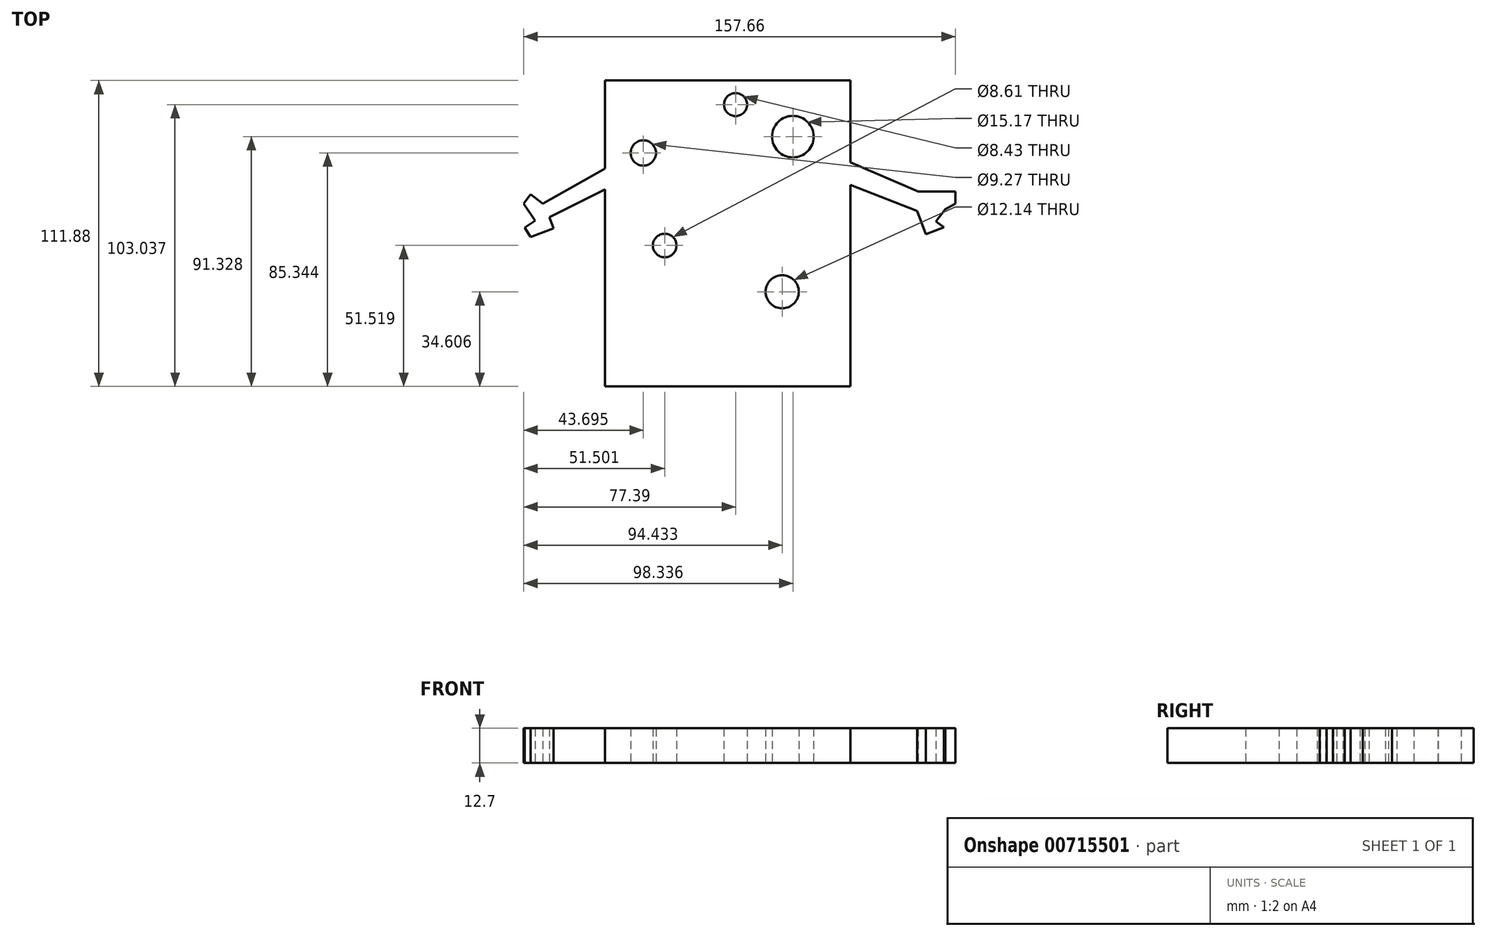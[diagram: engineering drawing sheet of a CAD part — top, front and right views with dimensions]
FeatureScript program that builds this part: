
annotation { "Feature Type Name" : "Feature", "Feature Type Description" : "" }
export const myFeature = defineFeature(function(context is Context, id is Id, definition is map)
    precondition{}
    {
        {
            var Q0;
            Q0=qCreatedBy(makeId("Top.planeOp"),FACE);
            var sketch = newSketch(context, id + "F0", { "sketchPlane" : qUnion([Q0])});
            skLineSegment(sketch, "E0.bottom", {"start": v(-47.75, 45.01) * mm, "end": v(42.02, 45.01) * mm});
            skLineSegment(sketch, "E0.top", {"start": v(-47.75, -66.87) * mm, "end": v(42.02, -66.87) * mm});
            skLineSegment(sketch, "E0.left", {"start": v(-47.75, 45.01) * mm, "end": v(-47.75, -66.87) * mm});
            skLineSegment(sketch, "E0.right", {"start": v(42.02, 45.01) * mm, "end": v(42.02, -66.87) * mm});
            skCircle(sketch, "E1", {"center": v(-33.7, 18.47) * mm, "radius": 4.63 * mm});
            skCircle(sketch, "E2", {"center": v(0, 36.17) * mm, "radius": 4.21 * mm});
            skCircle(sketch, "E3", {"center": v(20.95, 24.46) * mm, "radius": 7.59 * mm});
            skCircle(sketch, "E4", {"center": v(-25.89, -15.35) * mm, "radius": 4.3 * mm});
            skCircle(sketch, "E5", {"center": v(17.04, -32.26) * mm, "radius": 6.07 * mm});
            skLineSegment(sketch, "E6", {"start": v(-47.75, 12.75) * mm, "end": v(-70.38, 0) * mm});
            skLineSegment(sketch, "E7", {"start": v(-70.38, 0) * mm, "end": v(-74.8, 3.38) * mm});
            skLineSegment(sketch, "E8", {"start": v(-74.8, 3.38) * mm, "end": v(-77.4, 0) * mm});
            skLineSegment(sketch, "E9", {"start": v(-77.4, 0) * mm, "end": v(-73.24, -6.24) * mm});
            skLineSegment(sketch, "E10", {"start": v(-73.24, -6.24) * mm, "end": v(-77.1, -8.8) * mm});
            skLineSegment(sketch, "E11", {"start": v(-77.1, -8.8) * mm, "end": v(-74.81, -12.23) * mm});
            skLineSegment(sketch, "E12", {"start": v(-74.81, -12.23) * mm, "end": v(-66.48, -9.1) * mm});
            skLineSegment(sketch, "E13", {"start": v(-66.48, -9.1) * mm, "end": v(-68, -5.06) * mm});
            skLineSegment(sketch, "E14", {"start": v(-68, -5.06) * mm, "end": v(-47.75, 5.2) * mm});
            skLineSegment(sketch, "E15", {"start": v(42.02, 15.1) * mm, "end": v(66.74, 4.42) * mm});
            skLineSegment(sketch, "E16", {"start": v(66.74, 4.42) * mm, "end": v(80.27, 4.42) * mm});
            skLineSegment(sketch, "E17", {"start": v(80.27, 4.42) * mm, "end": v(80.27, 0) * mm});
            skLineSegment(sketch, "E18", {"start": v(80.27, 0) * mm, "end": v(76.63, -2.08) * mm});
            skLineSegment(sketch, "E19", {"start": v(76.63, -2.08) * mm, "end": v(73.24, -6.5) * mm});
            skLineSegment(sketch, "E20", {"start": v(73.24, -6.5) * mm, "end": v(76.18, -8.75) * mm});
            skLineSegment(sketch, "E21", {"start": v(76.18, -8.75) * mm, "end": v(69.48, -11.23) * mm});
            skLineSegment(sketch, "E22", {"start": v(69.48, -11.23) * mm, "end": v(66.34, -2.77) * mm});
            skLineSegment(sketch, "E23", {"start": v(66.34, -2.77) * mm, "end": v(42.02, 6.8) * mm});
            skSolve(sketch);
        }
        {
            var Q0;
            Q0 = qSketchRegion(id + "F0", true);
            extrude(context, id + "F1", {"entities" : qUnion([Q0]), "depth" : 12.7 * mm, "offsetDistance" : 25.4 * mm});
        }
    });
